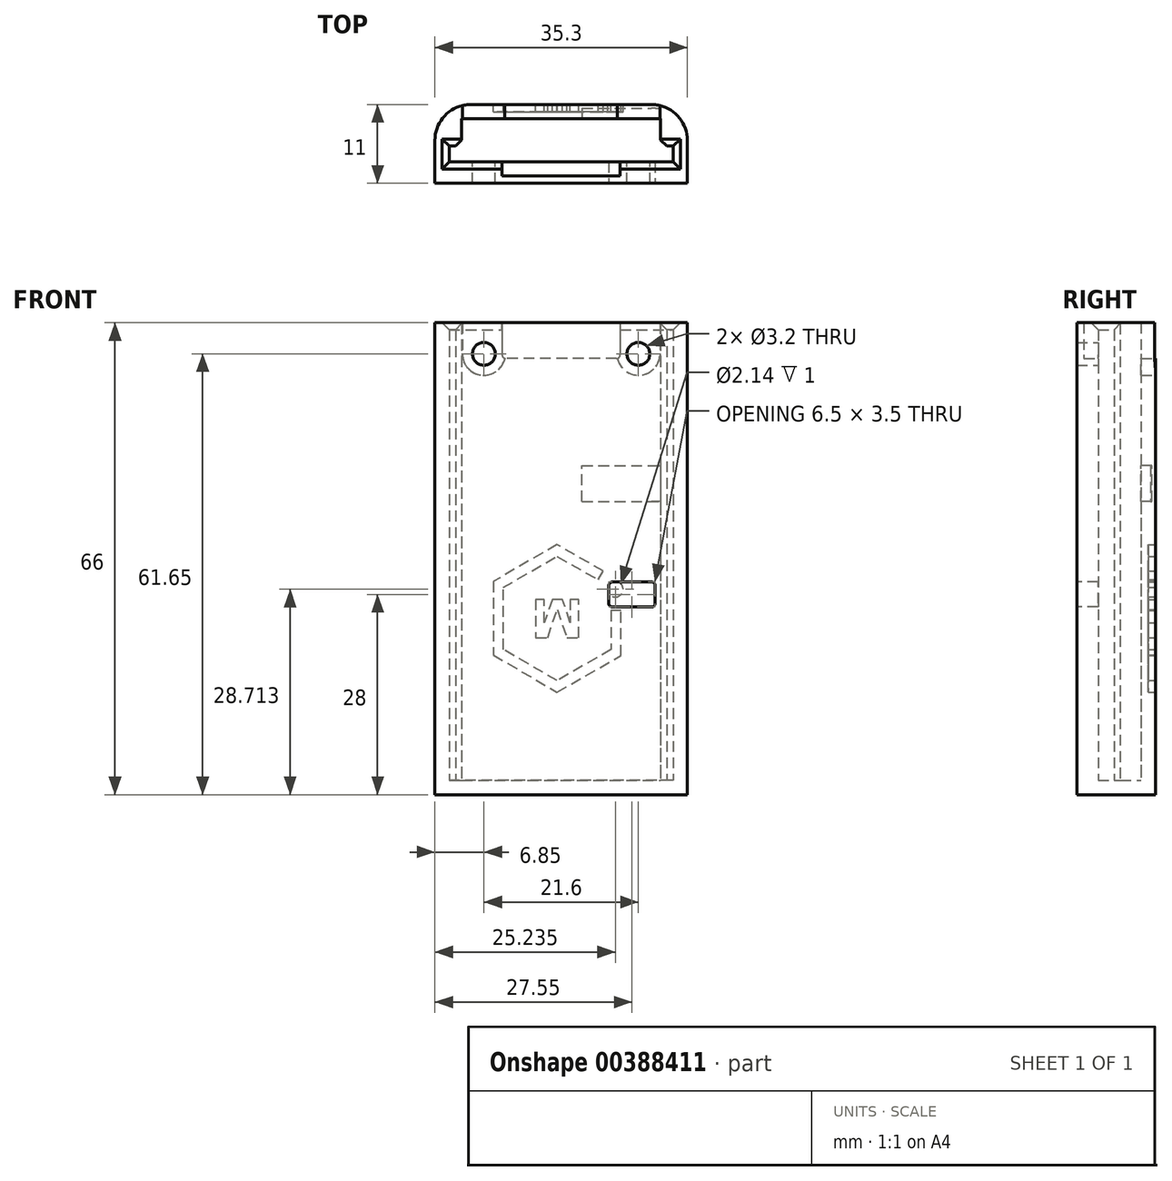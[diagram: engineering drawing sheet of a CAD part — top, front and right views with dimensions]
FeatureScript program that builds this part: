
annotation { "Feature Type Name" : "Feature", "Feature Type Description" : "" }
export const myFeature = defineFeature(function(context is Context, id is Id, definition is map)
    precondition{}
    {
        {
            var Q0;
            Q0=qCreatedBy(makeId("Top.planeOp"),FACE);
            var sketch = newSketch(context, id + "F0", { "sketchPlane" : qUnion([Q0])});
            skLineSegment(sketch, "E0.bottom", {"start": v(0, 0) * mm, "end": v(15.65, 0) * mm});
            skLineSegment(sketch, "E0.top", {"start": v(0, 2.2) * mm, "end": v(0.88, 2.2) * mm});
            skLineSegment(sketch, "E0.left", {"start": v(0, 0) * mm, "end": v(0, 2.2) * mm});
            skLineSegment(sketch, "E1.top", {"start": v(1.75, 6) * mm, "end": v(15.65, 6) * mm});
            skLineSegment(sketch, "E1.left", {"start": v(1.75, 3.07) * mm, "end": v(1.75, 6) * mm});
            skLineSegment(sketch, "E2", {"start": v(0.88, 2.2) * mm, "end": v(1.75, 3.07) * mm});
            skLineSegment(sketch, "E3", {"start": v(15.65, 6) * mm, "end": v(15.65, 0) * mm, "construction": true});
            skPoint(sketch, "E4.orphan", {"position": v(1.75, 2.2) * mm});
            skLineSegment(sketch, "E5.MirrorCS", {"start": v(29.55, 6) * mm, "end": v(15.65, 6) * mm});
            skLineSegment(sketch, "E6.MirrorCS", {"start": v(31.3, 0) * mm, "end": v(15.65, 0) * mm});
            skLineSegment(sketch, "E7.MirrorCS", {"start": v(29.55, 3.08) * mm, "end": v(29.55, 6) * mm});
            skPoint(sketch, "E8.MirrorP", {"position": v(29.55, 2.2) * mm});
            skLineSegment(sketch, "E9.MirrorCS", {"start": v(31.3, 2.2) * mm, "end": v(30.43, 2.2) * mm});
            skLineSegment(sketch, "E10.MirrorCS", {"start": v(30.43, 2.2) * mm, "end": v(29.55, 3.08) * mm});
            skLineSegment(sketch, "E11.MirrorCS", {"start": v(31.3, 0) * mm, "end": v(31.3, 2.2) * mm});
            skLineSegment(sketch, "E12", {"start": v(15.65, 8) * mm, "end": v(3, 8) * mm});
            skLineSegment(sketch, "E13", {"start": v(-2, 3) * mm, "end": v(-2, -3) * mm});
            skLineSegment(sketch, "E14", {"start": v(-2, -3) * mm, "end": v(15.65, -3) * mm});
            skPoint(sketch, "E15.visualSharp", {"position": v(-2, 8) * mm});
            skArc(sketch, "E15.filletArc", {"start": v(3, 8) * mm, "mid": v(-0.54, 6.54) * mm, "end": v(-2, 3) * mm});
            skLineSegment(sketch, "E16.MirrorCS", {"start": v(15.65, 8) * mm, "end": v(28.3, 8) * mm});
            skArc(sketch, "E17.MirrorCS", {"start": v(28.3, 8) * mm, "mid": v(31.84, 6.54) * mm, "end": v(33.3, 3) * mm});
            skLineSegment(sketch, "E18.MirrorCS", {"start": v(33.3, 3) * mm, "end": v(33.3, -3) * mm});
            skLineSegment(sketch, "E19.MirrorCS", {"start": v(33.3, -3) * mm, "end": v(15.65, -3) * mm});
            skSolve(sketch);
        }
        {
            var Q0;
            Q0 = qSketchRegion(id + "F0", true);
            extrude(context, id + "F1", {"entities" : qUnion([Q0]), "depth" : 64 * mm});
        }
        {
            var Q0;
            Q0=makeQuery(id+"F1.opExtrude","CAP_FACE",FACE,{"disambiguationData":[OSD([sQuery(id+"F0.wireOp",EDGE,"E0.bottom"),sQuery(id+"F0.wireOp",EDGE,"E0.top"),sQuery(id+"F0.wireOp",EDGE,"E0.left"),sQuery(id+"F0.wireOp",EDGE,"E1.top"),sQuery(id+"F0.wireOp",EDGE,"E1.left"),sQuery(id+"F0.wireOp",EDGE,"E2"),sQuery(id+"F0.wireOp",EDGE,"E5.MirrorCS"),sQuery(id+"F0.wireOp",EDGE,"E6.MirrorCS"),sQuery(id+"F0.wireOp",EDGE,"E7.MirrorCS"),sQuery(id+"F0.wireOp",EDGE,"E9.MirrorCS"),sQuery(id+"F0.wireOp",EDGE,"E10.MirrorCS"),sQuery(id+"F0.wireOp",EDGE,"E11.MirrorCS"),sQuery(id+"F0.wireOp",EDGE,"E12"),sQuery(id+"F0.wireOp",EDGE,"E13"),sQuery(id+"F0.wireOp",EDGE,"E14"),sQuery(id+"F0.wireOp",EDGE,"E15.filletArc"),sQuery(id+"F0.wireOp",EDGE,"E16.MirrorCS"),sQuery(id+"F0.wireOp",EDGE,"E17.MirrorCS"),sQuery(id+"F0.wireOp",EDGE,"E18.MirrorCS"),sQuery(id+"F0.wireOp",EDGE,"E19.MirrorCS")])],"isStart":true});
            var sketch = newSketch(context, id + "F2", { "sketchPlane" : qUnion([Q0])});
            skLineSegment(sketch, "E20.0", {"start": v(3, -8) * mm, "end": v(28.3, -8) * mm});
            skArc(sketch, "E21.0", {"start": v(28.3, -8) * mm, "mid": v(31.84, -6.54) * mm, "end": v(33.3, -3) * mm});
            skLineSegment(sketch, "E22.0", {"start": v(33.3, -3) * mm, "end": v(33.3, 3) * mm});
            skLineSegment(sketch, "E23.0", {"start": v(-2, 3) * mm, "end": v(33.3, 3) * mm});
            skLineSegment(sketch, "E24.0", {"start": v(-2, -3) * mm, "end": v(-2, 3) * mm});
            skArc(sketch, "E25.0", {"start": v(3, -8) * mm, "mid": v(-0.54, -6.54) * mm, "end": v(-2, -3) * mm});
            skSolve(sketch);
        }
        {
            var Q0;
            Q0 = qSketchRegion(id + "F2", true);
            extrude(context, id + "F3", {"entities" : qUnion([Q0]), "operationType" : NewBodyOperationType.ADD, "depth" : 2 * mm});
        }
        {
            var Q0;
            Q0=makeQuery(id+"F3.boolean.opBoolean","MERGE",FACE,{"derivedFrom":[makeQuery(id+"F1.opExtrude","SWEPT_FACE",FACE,{"disambiguationData":[OSD([sQuery(id+"F0.wireOp",EDGE,"E12"),sQuery(id+"F0.wireOp",EDGE,"E16.MirrorCS")])]}),makeQuery(id+"F3.opExtrude","SWEPT_FACE",FACE,{"disambiguationData":[OSD([sQuery(id+"F2.wireOp",EDGE,"E20.0")])]})]});
            var sketch = newSketch(context, id + "F4", { "sketchPlane" : qUnion([Q0])});
            skLineSegment(sketch, "E26", {"start": v(-15.65, 64) * mm, "end": v(-15.65, 28.72) * mm, "construction": true});
            skPoint(sketch, "E26.endSnap0", {"position": v(-15.65, 64) * mm});
            skLineSegment(sketch, "E27", {"start": v(-7.4, 64) * mm, "end": v(-7.4, 59.5) * mm});
            skLineSegment(sketch, "E28", {"start": v(-7.9, 59) * mm, "end": v(-15.65, 59) * mm});
            skLineSegment(sketch, "E29", {"start": v(-7.4, 64) * mm, "end": v(-15.65, 64) * mm});
            skLineSegment(sketch, "E30.MirrorCS", {"start": v(-23.4, 59) * mm, "end": v(-15.65, 59) * mm});
            skLineSegment(sketch, "E31.MirrorCS", {"start": v(-23.9, 64) * mm, "end": v(-15.65, 64) * mm});
            skLineSegment(sketch, "E32.MirrorCS", {"start": v(-23.9, 64) * mm, "end": v(-23.9, 59.5) * mm});
            skPoint(sketch, "E33.visualSharp", {"position": v(-7.4, 59) * mm});
            skArc(sketch, "E33.filletArc", {"start": v(-7.9, 59) * mm, "mid": v(-7.55, 59.15) * mm, "end": v(-7.4, 59.5) * mm});
            skPoint(sketch, "E34.visualSharp", {"position": v(-23.9, 59) * mm});
            skArc(sketch, "E34.filletArc", {"start": v(-23.9, 59.5) * mm, "mid": v(-23.75, 59.15) * mm, "end": v(-23.4, 59) * mm});
            skSolve(sketch);
        }
        {
            var Q0;
            Q0 = qSketchRegion(id + "F4", true);
            extrude(context, id + "F5", {"entities" : qUnion([Q0]), "operationType" : NewBodyOperationType.REMOVE, "endBound" : BoundingType.UP_TO_NEXT, "oppositeDirection" : true, "depth" : 25 * mm});
        }
        {
            var Q0;
            Q0=makeQuery(id+"F3.boolean.opBoolean","MERGE",FACE,{"derivedFrom":[makeQuery(id+"F1.opExtrude","SWEPT_FACE",FACE,{"disambiguationData":[OSD([sQuery(id+"F0.wireOp",EDGE,"E12"),sQuery(id+"F0.wireOp",EDGE,"E16.MirrorCS")])]}),makeQuery(id+"F3.opExtrude","SWEPT_FACE",FACE,{"disambiguationData":[OSD([sQuery(id+"F2.wireOp",EDGE,"E20.0")])]})]});
            var sketch = newSketch(context, id + "F6", { "sketchPlane" : qUnion([Q0])});
            skArc(sketch, "E35", {"start": v(-7.85, 59.65) * mm, "mid": v(-4.85, 56.65) * mm, "end": v(-1.85, 59.65) * mm});
            skLineSegment(sketch, "E36", {"start": v(-15.65, 56.1) * mm, "end": v(-15.65, 64) * mm, "construction": true});
            skLineSegment(sketch, "E37", {"start": v(-1.85, 59.65) * mm, "end": v(-1.85, 64.57) * mm});
            skLineSegment(sketch, "E38", {"start": v(-1.85, 64.57) * mm, "end": v(-7.85, 64.57) * mm});
            skLineSegment(sketch, "E39", {"start": v(-7.85, 64.57) * mm, "end": v(-7.85, 59.65) * mm});
            skArc(sketch, "E40.MirrorCS", {"start": v(-23.45, 59.65) * mm, "mid": v(-26.45, 56.65) * mm, "end": v(-29.45, 59.65) * mm});
            skLineSegment(sketch, "E41.MirrorCS", {"start": v(-23.45, 64.57) * mm, "end": v(-23.45, 59.65) * mm});
            skLineSegment(sketch, "E42.MirrorCS", {"start": v(-29.45, 64.57) * mm, "end": v(-23.45, 64.57) * mm});
            skLineSegment(sketch, "E43.MirrorCS", {"start": v(-29.45, 59.65) * mm, "end": v(-29.45, 64.57) * mm});
            skSolve(sketch);
        }
        {
            var Q0;
            Q0 = qSketchRegion(id + "F6", true);
            extrude(context, id + "F7", {"entities" : qUnion([Q0]), "operationType" : NewBodyOperationType.REMOVE, "endBound" : BoundingType.UP_TO_NEXT, "oppositeDirection" : true, "depth" : 25 * mm});
        }
        {
            var Q0;
            Q0=makeQuery(id+"F1.opExtrude","SWEPT_FACE",FACE,{"disambiguationData":[OSD([sQuery(id+"F0.wireOp",EDGE,"E0.bottom"),sQuery(id+"F0.wireOp",EDGE,"E6.MirrorCS")])]});
            var sketch = newSketch(context, id + "F8", { "sketchPlane" : qUnion([Q0])});
            skLineSegment(sketch, "E44", {"start": v(-15.65, 64) * mm, "end": v(-15.65, 28.72) * mm, "construction": true});
            skPoint(sketch, "E44.endSnap0", {"position": v(-15.65, 64) * mm});
            skLineSegment(sketch, "E45", {"start": v(-7.4, 64) * mm, "end": v(-7.4, 59.5) * mm});
            skLineSegment(sketch, "E46", {"start": v(-7.9, 59) * mm, "end": v(-15.65, 59) * mm});
            skLineSegment(sketch, "E47", {"start": v(-7.4, 64) * mm, "end": v(-15.65, 64) * mm});
            skLineSegment(sketch, "E48.MirrorCS", {"start": v(-23.4, 59) * mm, "end": v(-15.65, 59) * mm});
            skLineSegment(sketch, "E49.MirrorCS", {"start": v(-23.9, 64) * mm, "end": v(-15.65, 64) * mm});
            skLineSegment(sketch, "E50.MirrorCS", {"start": v(-23.9, 64) * mm, "end": v(-23.9, 59.5) * mm});
            skPoint(sketch, "E51.visualSharp", {"position": v(-7.4, 59) * mm});
            skArc(sketch, "E51.filletArc", {"start": v(-7.9, 59) * mm, "mid": v(-7.55, 59.15) * mm, "end": v(-7.4, 59.5) * mm});
            skPoint(sketch, "E52.visualSharp", {"position": v(-23.9, 59) * mm});
            skArc(sketch, "E52.filletArc", {"start": v(-23.9, 59.5) * mm, "mid": v(-23.75, 59.15) * mm, "end": v(-23.4, 59) * mm});
            skSolve(sketch);
        }
        {
            var Q0;
            Q0 = qSketchRegion(id + "F8", true);
            extrude(context, id + "F9", {"entities" : qUnion([Q0]), "operationType" : NewBodyOperationType.REMOVE, "oppositeDirection" : true, "depth" : 2 * mm});
        }
        {
            var Q0;
            {var subQ0=sQuery(id+"F0.wireOp",EDGE,"E6.MirrorCS");var subQ1=sQuery(id+"F0.wireOp",EDGE,"E0.left");var subQ2=sQuery(id+"F0.wireOp",EDGE,"E0.bottom");Q0=makeQuery(id+"F9.boolean.opBoolean","SPLIT",EDGE,{"disambiguationData":[TD([makeQuery(id+"F1.opExtrude","SWEPT_FACE",FACE,{"disambiguationData":[OSD([subQ1])]})])],"derivedFrom":makeQuery(id+"F1.opExtrude","CAP_EDGE",EDGE,{"disambiguationData":[OSD([subQ2,subQ0])],"isStart":false})});}
            var Q1;
            {var subQ0=sQuery(id+"F0.wireOp",EDGE,"E11.MirrorCS");var subQ1=sQuery(id+"F0.wireOp",EDGE,"E6.MirrorCS");var subQ2=sQuery(id+"F0.wireOp",EDGE,"E0.bottom");Q1=makeQuery(id+"F9.boolean.opBoolean","SPLIT",EDGE,{"disambiguationData":[TD([makeQuery(id+"F1.opExtrude","SWEPT_FACE",FACE,{"disambiguationData":[OSD([subQ0])]})])],"derivedFrom":makeQuery(id+"F1.opExtrude","CAP_EDGE",EDGE,{"disambiguationData":[OSD([subQ2,subQ1])],"isStart":false})});}
            var Q2;
            Q2=makeQuery(id+"F1.opExtrude","CAP_EDGE",EDGE,{"disambiguationData":[OSD([sQuery(id+"F0.wireOp",EDGE,"E0.left")])],"isStart":false});
            var Q3;
            Q3=makeQuery(id+"F1.opExtrude","CAP_EDGE",EDGE,{"disambiguationData":[OSD([sQuery(id+"F0.wireOp",EDGE,"E0.top")])],"isStart":false});
            var Q4;
            Q4=makeQuery(id+"F1.opExtrude","CAP_EDGE",EDGE,{"disambiguationData":[OSD([sQuery(id+"F0.wireOp",EDGE,"E11.MirrorCS")])],"isStart":false});
            var Q5;
            Q5=makeQuery(id+"F1.opExtrude","CAP_EDGE",EDGE,{"disambiguationData":[OSD([sQuery(id+"F0.wireOp",EDGE,"E9.MirrorCS")])],"isStart":false});
            chamfer(context, id + "F10", {"entities" : qUnion([Q0, Q1, Q2, Q3, Q4, Q5]), "width" : 1 * mm, "tangentPropagation" : true});
        }
        {
            var Q0;
            Q0=makeQuery(id+"F1.opExtrude","SWEPT_FACE",FACE,{"disambiguationData":[OSD([sQuery(id+"F0.wireOp",EDGE,"E0.bottom"),sQuery(id+"F0.wireOp",EDGE,"E6.MirrorCS")])]});
            var sketch = newSketch(context, id + "F11", { "sketchPlane" : qUnion([Q0])});
            skCircle(sketch, "E53", {"center": v(-4.85, 59.65) * mm, "radius": 1.6 * mm});
            skLineSegment(sketch, "E54", {"start": v(-15.65, 64) * mm, "end": v(-15.65, 53.7) * mm, "construction": true});
            skCircle(sketch, "E55.MirrorC", {"center": v(-26.45, 59.65) * mm, "radius": 1.6 * mm});
            skSolve(sketch);
        }
        {
            var Q0;
            Q0 = qSketchRegion(id + "F11", true);
            extrude(context, id + "F12", {"entities" : qUnion([Q0]), "operationType" : NewBodyOperationType.REMOVE, "endBound" : BoundingType.THROUGH_ALL, "oppositeDirection" : true, "depth" : 25 * mm});
        }
        {
            var Q0;
            Q0=makeQuery(id+"F1.opExtrude","SWEPT_FACE",FACE,{"disambiguationData":[OSD([sQuery(id+"F0.wireOp",EDGE,"E1.top"),sQuery(id+"F0.wireOp",EDGE,"E5.MirrorCS")])]});
            var sketch = newSketch(context, id + "F13", { "sketchPlane" : qUnion([Q0])});
            skLineSegment(sketch, "E56.bottom", {"start": v(18.55, 39) * mm, "end": v(29.55, 39) * mm});
            skLineSegment(sketch, "E56.top", {"start": v(18.55, 44) * mm, "end": v(29.55, 44) * mm});
            skLineSegment(sketch, "E56.left", {"start": v(18.55, 39) * mm, "end": v(18.55, 44) * mm});
            skLineSegment(sketch, "E56.right", {"start": v(29.55, 39) * mm, "end": v(29.55, 44) * mm});
            skSolve(sketch);
        }
        {
            var Q0;
            Q0 = qSketchRegion(id + "F13", true);
            extrude(context, id + "F14", {"entities" : qUnion([Q0]), "operationType" : NewBodyOperationType.REMOVE, "oppositeDirection" : true, "depth" : 1.5 * mm});
        }
        {
            var Q0;
            Q0=makeQuery(id+"F14.boolean.opBoolean","COPY",FACE,{"derivedFrom":makeQuery(id+"F14.opExtrude","SWEPT_FACE",FACE,{"disambiguationData":[OSD([sQuery(id+"F13.wireOp",EDGE,"E56.bottom")])]})});
            var sketch = newSketch(context, id + "F15", { "sketchPlane" : qUnion([Q0])});
            skArc(sketch, "E57.0", {"start": v(28.3, 7.5) * mm, "mid": v(28.93, 7.46) * mm, "end": v(29.55, 7.32) * mm});
            skLineSegment(sketch, "E58", {"start": v(28.3, 7.5) * mm, "end": v(29.55, 7.5) * mm});
            skLineSegment(sketch, "E59", {"start": v(29.55, 7.5) * mm, "end": v(29.55, 7.32) * mm});
            skSolve(sketch);
        }
        {
            var Q0;
            Q0 = qSketchRegion(id + "F15", true);
            extrude(context, id + "F16", {"entities" : qUnion([Q0]), "operationType" : NewBodyOperationType.ADD, "endBound" : BoundingType.UP_TO_NEXT, "depth" : 25 * mm});
        }
        {
            var Q0;
            Q0=makeQuery(id+"F3.boolean.opBoolean","MERGE",FACE,{"derivedFrom":[makeQuery(id+"F1.opExtrude","SWEPT_FACE",FACE,{"disambiguationData":[OSD([sQuery(id+"F0.wireOp",EDGE,"E12"),sQuery(id+"F0.wireOp",EDGE,"E16.MirrorCS")])]}),makeQuery(id+"F3.opExtrude","SWEPT_FACE",FACE,{"disambiguationData":[OSD([sQuery(id+"F2.wireOp",EDGE,"E20.0")])]})]});
            var sketch = newSketch(context, id + "F17", { "sketchPlane" : qUnion([Q0])});
            skLineSegment(sketch, "E60", {"start": v(-21.56, 29.27) * mm, "end": v(-15.07, 32.97) * mm});
            skLineSegment(sketch, "E61", {"start": v(-15.07, 32.97) * mm, "end": v(-6.16, 27.82) * mm});
            skLineSegment(sketch, "E62", {"start": v(-6.16, 27.82) * mm, "end": v(-6.16, 17.52) * mm});
            skLineSegment(sketch, "E63", {"start": v(-6.16, 17.52) * mm, "end": v(-15.08, 12.34) * mm});
            skLineSegment(sketch, "E64", {"start": v(-15.08, 12.34) * mm, "end": v(-24.04, 17.46) * mm});
            skLineSegment(sketch, "E65", {"start": v(-24.04, 17.46) * mm, "end": v(-24.04, 23.73) * mm});
            skLineSegment(sketch, "E66", {"start": v(-24.04, 23.73) * mm, "end": v(-22.63, 23.73) * mm});
            skLineSegment(sketch, "E67", {"start": v(-22.63, 23.73) * mm, "end": v(-22.63, 18.32) * mm});
            skLineSegment(sketch, "E68", {"start": v(-22.63, 18.32) * mm, "end": v(-15.08, 13.95) * mm});
            skLineSegment(sketch, "E69", {"start": v(-15.08, 13.95) * mm, "end": v(-7.56, 18.3) * mm});
            skLineSegment(sketch, "E70", {"start": v(-7.56, 18.3) * mm, "end": v(-7.56, 26.98) * mm});
            skLineSegment(sketch, "E71", {"start": v(-7.56, 26.98) * mm, "end": v(-15.08, 31.32) * mm});
            skLineSegment(sketch, "E72", {"start": v(-15.08, 31.32) * mm, "end": v(-20.83, 28.05) * mm});
            skLineSegment(sketch, "E73", {"start": v(-20.83, 28.05) * mm, "end": v(-21.56, 29.27) * mm});
            skCircle(sketch, "E74", {"center": v(-23.24, 26.71) * mm, "radius": 1.07 * mm});
            skLineSegment(sketch, "E75", {"start": v(-12.09, 25.31) * mm, "end": v(-12.09, 19.97) * mm});
            skLineSegment(sketch, "E76", {"start": v(-12.09, 19.97) * mm, "end": v(-13.77, 19.97) * mm});
            skLineSegment(sketch, "E77", {"start": v(-13.77, 19.97) * mm, "end": v(-15.12, 23.92) * mm});
            skLineSegment(sketch, "E78", {"start": v(-15.12, 23.92) * mm, "end": v(-16.43, 19.97) * mm});
            skLineSegment(sketch, "E79", {"start": v(-16.43, 19.97) * mm, "end": v(-18.12, 19.97) * mm});
            skLineSegment(sketch, "E80", {"start": v(-18.12, 19.97) * mm, "end": v(-18.12, 25.3) * mm});
            skLineSegment(sketch, "E81", {"start": v(-18.12, 25.3) * mm, "end": v(-16.91, 25.3) * mm});
            skLineSegment(sketch, "E82", {"start": v(-16.91, 25.3) * mm, "end": v(-16.91, 22.06) * mm});
            skLineSegment(sketch, "E83", {"start": v(-16.91, 22.06) * mm, "end": v(-15.82, 25.3) * mm});
            skLineSegment(sketch, "E84", {"start": v(-15.82, 25.3) * mm, "end": v(-14.4, 25.3) * mm});
            skLineSegment(sketch, "E85", {"start": v(-14.4, 25.3) * mm, "end": v(-13.3, 22.07) * mm});
            skLineSegment(sketch, "E86", {"start": v(-13.3, 22.07) * mm, "end": v(-13.3, 25.3) * mm});
            skLineSegment(sketch, "E87", {"start": v(-13.3, 25.3) * mm, "end": v(-12.09, 25.31) * mm});
            skSolve(sketch);
        }
        {
            var Q0;
            Q0 = qSketchRegion(id + "F17", true);
            extrude(context, id + "F18", {"entities" : qUnion([Q0]), "operationType" : NewBodyOperationType.REMOVE, "oppositeDirection" : true, "depth" : 1 * mm});
        }
        {
            var Q0;
            Q0=makeQuery(id+"F3.boolean.opBoolean","MERGE",FACE,{"derivedFrom":[makeQuery(id+"F1.opExtrude","SWEPT_FACE",FACE,{"disambiguationData":[OSD([sQuery(id+"F0.wireOp",EDGE,"E14"),sQuery(id+"F0.wireOp",EDGE,"E19.MirrorCS")])]}),makeQuery(id+"F3.opExtrude","SWEPT_FACE",FACE,{"disambiguationData":[OSD([sQuery(id+"F2.wireOp",EDGE,"E23.0")])]})]});
            var sketch = newSketch(context, id + "F19", { "sketchPlane" : qUnion([Q0])});
            skLineSegment(sketch, "E88.bottom", {"start": v(22.8, 27.75) * mm, "end": v(28.3, 27.75) * mm});
            skLineSegment(sketch, "E88.top", {"start": v(22.8, 24.25) * mm, "end": v(28.3, 24.25) * mm});
            skLineSegment(sketch, "E88.left", {"start": v(22.3, 27.25) * mm, "end": v(22.3, 24.75) * mm});
            skLineSegment(sketch, "E88.right", {"start": v(28.8, 27.25) * mm, "end": v(28.8, 24.75) * mm});
            skPoint(sketch, "E89.visualSharp", {"position": v(22.3, 27.75) * mm});
            skArc(sketch, "E89.filletArc", {"start": v(22.8, 27.75) * mm, "mid": v(22.45, 27.6) * mm, "end": v(22.3, 27.25) * mm});
            skPoint(sketch, "E90.visualSharp", {"position": v(28.8, 27.75) * mm});
            skArc(sketch, "E90.filletArc", {"start": v(28.8, 27.25) * mm, "mid": v(28.65, 27.6) * mm, "end": v(28.3, 27.75) * mm});
            skPoint(sketch, "E91.visualSharp", {"position": v(28.8, 24.25) * mm});
            skArc(sketch, "E91.filletArc", {"start": v(28.3, 24.25) * mm, "mid": v(28.65, 24.4) * mm, "end": v(28.8, 24.75) * mm});
            skPoint(sketch, "E92.visualSharp", {"position": v(22.3, 24.25) * mm});
            skArc(sketch, "E92.filletArc", {"start": v(22.3, 24.75) * mm, "mid": v(22.45, 24.4) * mm, "end": v(22.8, 24.25) * mm});
            skSolve(sketch);
        }
        {
            var Q0;
            Q0 = qSketchRegion(id + "F19", true);
            extrude(context, id + "F20", {"entities" : qUnion([Q0]), "operationType" : NewBodyOperationType.REMOVE, "endBound" : BoundingType.UP_TO_NEXT, "oppositeDirection" : true, "depth" : 25 * mm});
        }
    });
